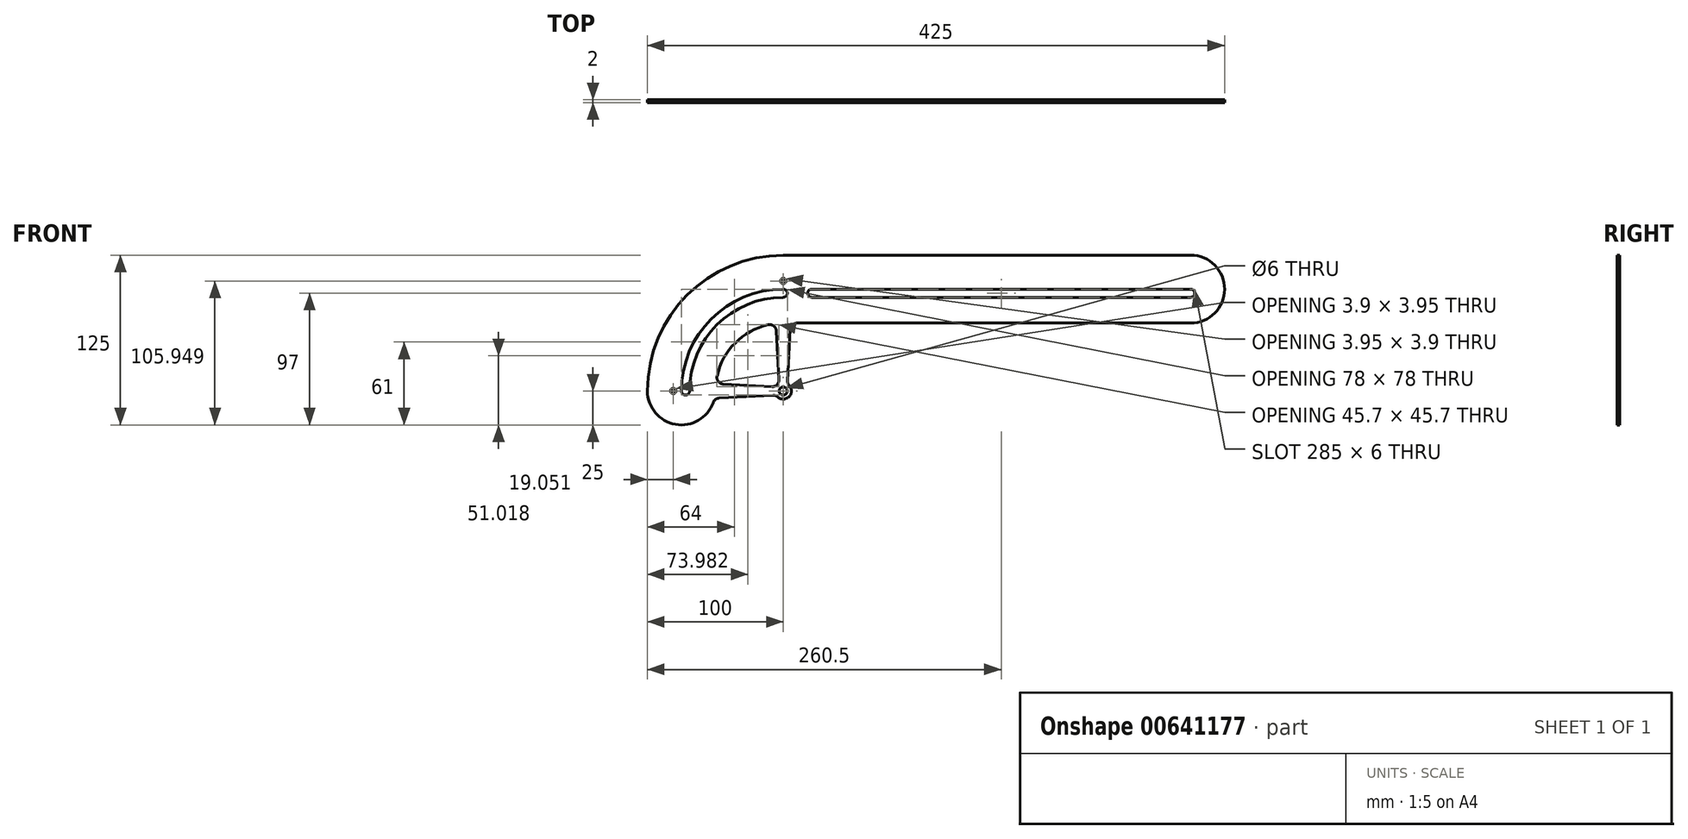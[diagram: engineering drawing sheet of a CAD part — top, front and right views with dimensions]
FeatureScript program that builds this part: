
annotation { "Feature Type Name" : "Feature", "Feature Type Description" : "" }
export const myFeature = defineFeature(function(context is Context, id is Id, definition is map)
    precondition{}
    {
        {
            var Q0;
            Q0=qCreatedBy(makeId("Front.planeOp"),FACE);
            var sketch = newSketch(context, id + "F0", { "sketchPlane" : qUnion([Q0])});
            skCircle(sketch, "E0", {"center": v(0, 0) * mm, "radius": 100 * mm, "construction": true});
            skCircle(sketch, "E1", {"center": v(0, 0) * mm, "radius": 75 * mm, "construction": true});
            skLineSegment(sketch, "E2", {"start": v(0, 0) * mm, "end": v(-100, 0) * mm, "construction": true});
            skLineSegment(sketch, "E3", {"start": v(0, 100) * mm, "end": v(300, 100) * mm});
            skArc(sketch, "E4", {"start": v(-50, 0) * mm, "mid": v(49.93, -2.67) * mm, "end": v(-49.71, 5.33) * mm, "construction": true});
            skLineSegment(sketch, "E5", {"start": v(0, 50) * mm, "end": v(300, 50) * mm});
            skCircle(sketch, "E6", {"center": v(-72, 0) * mm, "radius": 3 * mm});
            skCircle(sketch, "E7", {"center": v(0, 72) * mm, "radius": 3 * mm});
            skArc(sketch, "E8", {"start": v(-75, 0) * mm, "mid": v(-53.03, 53.03) * mm, "end": v(0, 75) * mm});
            skArc(sketch, "E9", {"start": v(-69, 0) * mm, "mid": v(-48.8, 48.8) * mm, "end": v(0, 69) * mm});
            skLineSegment(sketch, "E10", {"start": v(0, 75) * mm, "end": v(300, 75) * mm, "construction": true});
            skCircle(sketch, "E11", {"center": v(-75, 0) * mm, "radius": 25 * mm});
            skArc(sketch, "E12", {"start": v(-100, 0) * mm, "mid": v(-70.71, 70.71) * mm, "end": v(0, 100) * mm});
            skArc(sketch, "E13", {"start": v(-50, 0) * mm, "mid": v(-35.36, 35.36) * mm, "end": v(0, 50) * mm});
            skCircle(sketch, "E14", {"center": v(300, 72) * mm, "radius": 3 * mm});
            skCircle(sketch, "E15", {"center": v(21, 72) * mm, "radius": 3 * mm});
            skCircle(sketch, "E16", {"center": v(300, 75) * mm, "radius": 25 * mm});
            skCircle(sketch, "E17", {"center": v(0, 0) * mm, "radius": 6 * mm});
            skCircle(sketch, "E18", {"center": v(0, 0) * mm, "radius": 3 * mm});
            skLineSegment(sketch, "E19", {"start": v(-50.59, -5.38) * mm, "end": v(-5.2, -3) * mm});
            skLineSegment(sketch, "E20", {"start": v(-5.2, 3) * mm, "end": v(-49.71, 5.33) * mm});
            skLineSegment(sketch, "E21", {"start": v(-5.2, 3) * mm, "end": v(-5.2, -3) * mm, "construction": true});
            skLineSegment(sketch, "E22", {"start": v(0, 0) * mm, "end": v(0, 72) * mm, "construction": true});
            skLineSegment(sketch, "E23", {"start": v(-3, 5.2) * mm, "end": v(-5.33, 49.71) * mm});
            skLineSegment(sketch, "E24", {"start": v(3, 5.2) * mm, "end": v(5.35, 50) * mm});
            skLineSegment(sketch, "E25", {"start": v(-3, 5.2) * mm, "end": v(3, 5.2) * mm, "construction": true});
            skLineSegment(sketch, "E26", {"start": v(300, 75) * mm, "end": v(21, 75) * mm});
            skLineSegment(sketch, "E27", {"start": v(21, 69) * mm, "end": v(300, 69) * mm});
            skSolve(sketch);
        }
        {
            var Q0;
            {var subQ1=sQuery(id+"F0.wireOp",EDGE,"E6");var subQ6=sQuery(id+"F0.wireOp",EDGE,"E8");var subQ8=makeQuery(id+"F0.imprint","INTERSECT",VERTEX,{"derivedFrom":[subQ1,subQ6]});Q0=makeQuery(id+"F0.imprint","IMPRINT",FACE,{"disambiguationData":[TD([[makeQuery(id+"F0.imprint","IMPRINT",EDGE,{"disambiguationData":[TD([[subQ8,-1.0]])],"derivedFrom":subQ1}),-1.0]])]});}
            var Q1;
            {var subQ0=sQuery(id+"F0.wireOp",EDGE,"E19");Q1=makeQuery(id+"F0.imprint","IMPRINT",FACE,{"disambiguationData":[TD([[makeQuery(id+"F0.imprint","IMPRINT",EDGE,{"derivedFrom":subQ0}),1.0]])]});}
            var Q2;
            {var subQ11=sQuery(id+"F0.wireOp",EDGE,"E3");Q2=makeQuery(id+"F0.imprint","IMPRINT",FACE,{"disambiguationData":[TD([[makeQuery(id+"F0.imprint","IMPRINT",EDGE,{"derivedFrom":subQ11}),-1.0]])]});}
            var Q3;
            {var subQ0=sQuery(id+"F0.wireOp",EDGE,"E23");Q3=makeQuery(id+"F0.imprint","IMPRINT",FACE,{"disambiguationData":[TD([[makeQuery(id+"F0.imprint","IMPRINT",EDGE,{"derivedFrom":subQ0}),-1.0]])]});}
            var Q4;
            Q4=makeQuery(id+"F0.imprint","IMPRINT",FACE,{"disambiguationData":[TD([[makeQuery(id+"F0.imprint","IMPRINT",EDGE,{"derivedFrom":sQuery(id+"F0.wireOp",EDGE,"E18")}),-1.0]])]});
            var Q5;
            {var subQ0=sQuery(id+"F0.wireOp",EDGE,"E16");var subQ1=makeQuery(id+"F0.imprint","INTERSECT",VERTEX,{"derivedFrom":[sQuery(id+"F0.wireOp",EDGE,"E3"),subQ0]});Q5=makeQuery(id+"F0.imprint","IMPRINT",FACE,{"disambiguationData":[TD([[makeQuery(id+"F0.imprint","IMPRINT",EDGE,{"disambiguationData":[TD([[subQ1,-1.0]])],"derivedFrom":subQ0}),1.0]])]});}
            extrude(context, id + "F1", {"entities" : qUnion([Q0, Q1, Q2, Q3, Q4, Q5]), "depth" : 2 * mm, "offsetDistance" : 25 * mm, "symmetric" : true});
        }
        {
            var Q0;
            Q0=makeQuery(id+"F1.opExtrude","SWEPT_EDGE",EDGE,{"disambiguationData":[OSD([sQuery(id+"F0.wireOp",EDGE,"E13"),sQuery(id+"F0.wireOp",EDGE,"E20")])]});
            var Q1;
            Q1=makeQuery(id+"F1.opExtrude","SWEPT_EDGE",EDGE,{"disambiguationData":[OSD([sQuery(id+"F0.wireOp",EDGE,"E5"),sQuery(id+"F0.wireOp",EDGE,"E24")])]});
            var Q2;
            Q2=makeQuery(id+"F1.opExtrude","SWEPT_EDGE",EDGE,{"disambiguationData":[OSD([sQuery(id+"F0.wireOp",EDGE,"E13"),sQuery(id+"F0.wireOp",EDGE,"E23")])]});
            var Q3;
            Q3=makeQuery(id+"F1.opExtrude","SWEPT_EDGE",EDGE,{"disambiguationData":[OSD([sQuery(id+"F0.wireOp",EDGE,"E17"),sQuery(id+"F0.wireOp",EDGE,"E19")])]});
            var Q4;
            Q4=makeQuery(id+"F1.opExtrude","SWEPT_EDGE",EDGE,{"disambiguationData":[OSD([sQuery(id+"F0.wireOp",EDGE,"E11"),sQuery(id+"F0.wireOp",EDGE,"E19")])]});
            var Q5;
            Q5=makeQuery(id+"F1.opExtrude","SWEPT_EDGE",EDGE,{"disambiguationData":[OSD([sQuery(id+"F0.wireOp",EDGE,"E17"),sQuery(id+"F0.wireOp",EDGE,"E20")])]});
            var Q6;
            Q6=makeQuery(id+"F1.opExtrude","SWEPT_EDGE",EDGE,{"disambiguationData":[OSD([sQuery(id+"F0.wireOp",EDGE,"E17"),sQuery(id+"F0.wireOp",EDGE,"E23")])]});
            var Q7;
            Q7=makeQuery(id+"F1.opExtrude","SWEPT_EDGE",EDGE,{"disambiguationData":[OSD([sQuery(id+"F0.wireOp",EDGE,"E17"),sQuery(id+"F0.wireOp",EDGE,"E24")])]});
            fillet(context, id + "F2", {"entities" : qUnion([Q0, Q1, Q2, Q3, Q4, Q5, Q6, Q7]), "radius" : 5 * mm, "tangentPropagation" : true, "allowEdgeOverflow" : false});
        }
        {
            var Q0;
            {var subQ0=sQuery(id+"F0.wireOp",EDGE,"E17");Q0=makeQuery(id+"F2.opFillet","BLEND_EDGE",EDGE,{"blendedFrom":[makeQuery(id+"F1.opExtrude","SWEPT_EDGE",EDGE,{"disambiguationData":[OSD([subQ0,sQuery(id+"F0.wireOp",EDGE,"E20")])]}),makeQuery(id+"F1.opExtrude","SWEPT_EDGE",EDGE,{"disambiguationData":[OSD([subQ0,sQuery(id+"F0.wireOp",EDGE,"E23")])]})],"blendedInto":[]});}
            fillet(context, id + "F3", {"entities" : qUnion([Q0]), "radius" : 5 * mm, "tangentPropagation" : true, "allowEdgeOverflow" : false});
        }
        {
            var Q0;
            Q0=makeQuery(id+"F1.opExtrude","CAP_FACE",FACE,{"disambiguationData":[OSD([sQuery(id+"F0.wireOp",EDGE,"E3"),sQuery(id+"F0.wireOp",EDGE,"E5"),sQuery(id+"F0.wireOp",EDGE,"E6"),sQuery(id+"F0.wireOp",EDGE,"E7"),sQuery(id+"F0.wireOp",EDGE,"E8"),sQuery(id+"F0.wireOp",EDGE,"E9"),sQuery(id+"F0.wireOp",EDGE,"E11"),sQuery(id+"F0.wireOp",EDGE,"E12"),sQuery(id+"F0.wireOp",EDGE,"E13"),sQuery(id+"F0.wireOp",EDGE,"E14"),sQuery(id+"F0.wireOp",EDGE,"E15"),sQuery(id+"F0.wireOp",EDGE,"E16"),sQuery(id+"F0.wireOp",EDGE,"E17"),sQuery(id+"F0.wireOp",EDGE,"E18"),sQuery(id+"F0.wireOp",EDGE,"E19"),sQuery(id+"F0.wireOp",EDGE,"E20"),sQuery(id+"F0.wireOp",EDGE,"E23"),sQuery(id+"F0.wireOp",EDGE,"E24"),sQuery(id+"F0.wireOp",EDGE,"E26"),sQuery(id+"F0.wireOp",EDGE,"E27")])],"isStart":false});
            var sketch = newSketch(context, id + "F4", { "sketchPlane" : qUnion([Q0])});
            skLineSegment(sketch, "E28", {"start": v(0, 0) * mm, "end": v(-83, 0) * mm});
            skLineSegment(sketch, "E29.1.0", {"start": v(-77.17, 7.15) * mm, "end": v(-82.65, 7.66) * mm});
            skLineSegment(sketch, "E29.2.0", {"start": v(-76.18, 14.24) * mm, "end": v(-81.59, 15.25) * mm});
            skLineSegment(sketch, "E29.3.0", {"start": v(-74.54, 21.2) * mm, "end": v(-79.83, 22.71) * mm});
            skLineSegment(sketch, "E29.4.0", {"start": v(-72.27, 28) * mm, "end": v(-77.4, 29.98) * mm});
            skLineSegment(sketch, "E29.5.0", {"start": v(-69.38, 34.54) * mm, "end": v(-74.3, 37) * mm});
            skLineSegment(sketch, "E29.6.0", {"start": v(-65.9, 40.8) * mm, "end": v(-70.57, 43.7) * mm});
            skLineSegment(sketch, "E29.7.0", {"start": v(-61.85, 46.7) * mm, "end": v(-66.24, 50.02) * mm});
            skLineSegment(sketch, "E29.8.0", {"start": v(-57.27, 52.21) * mm, "end": v(-61.34, 55.92) * mm});
            skLineSegment(sketch, "E29.9.0", {"start": v(-52.21, 57.27) * mm, "end": v(-55.92, 61.34) * mm});
            skLineSegment(sketch, "E29.10.0", {"start": v(-46.7, 61.85) * mm, "end": v(-50.02, 66.24) * mm});
            skLineSegment(sketch, "E29.11.0", {"start": v(-40.8, 65.9) * mm, "end": v(-43.7, 70.57) * mm});
            skLineSegment(sketch, "E29.12.0", {"start": v(-34.54, 69.38) * mm, "end": v(-37, 74.3) * mm});
            skLineSegment(sketch, "E29.13.0", {"start": v(-28, 72.27) * mm, "end": v(-29.98, 77.4) * mm});
            skLineSegment(sketch, "E29.14.0", {"start": v(-21.2, 74.54) * mm, "end": v(-22.71, 79.83) * mm});
            skLineSegment(sketch, "E29.15.0", {"start": v(-14.24, 76.18) * mm, "end": v(-15.25, 81.59) * mm});
            skLineSegment(sketch, "E29.16.0", {"start": v(-7.15, 77.17) * mm, "end": v(-7.66, 82.65) * mm});
            skLineSegment(sketch, "E29.17.0", {"start": v(0, 0) * mm, "end": v(0, 83) * mm});
            skPoint(sketch, "E29.center", {"position": v(0, 0) * mm});
            skLineSegment(sketch, "E29.anchor1", {"start": v(0, 0) * mm, "end": v(-83, 0) * mm, "construction": true});
            skLineSegment(sketch, "E29.anchor2", {"start": v(0, 0) * mm, "end": v(0, 83) * mm, "construction": true});
            skCircle(sketch, "E30", {"center": v(0, 0) * mm, "radius": 77.5 * mm, "construction": true});
            skSolve(sketch);
        }
        {
            var Q0;
            {var subQ19=sQuery(id+"F0.wireOp",EDGE,"E3");Q0=makeQuery(id+"F4.imprint","IMPRINT",FACE,{"disambiguationData":[TD([[makeQuery(id+"F4.imprint","IMPRINT",EDGE,{"derivedFrom":makeQuery(id+"F1.opExtrude","CAP_EDGE",EDGE,{"disambiguationData":[OSD([subQ19])],"isStart":false})}),-1.0]])]});}
            var sketch = newSketch(context, id + "F5", { "sketchPlane" : qUnion([Q0])});
            skCircle(sketch, "E31", {"center": v(-81, 0) * mm, "radius": 2 * mm});
            skLineSegment(sketch, "E32", {"start": v(-82.9, 0.63) * mm, "end": v(-82, 0) * mm});
            skLineSegment(sketch, "E33", {"start": v(-82, 0) * mm, "end": v(-82.9, -0.63) * mm});
            skPoint(sketch, "E34.orphan", {"position": v(-83.85, 1.3) * mm});
            skPoint(sketch, "E35.orphan", {"position": v(-83.85, -1.3) * mm});
            skLineSegment(sketch, "E36", {"start": v(-82, 0) * mm, "end": v(-81, 0) * mm, "construction": true});
            skCircle(sketch, "E37.1.0", {"center": v(0, 81) * mm, "radius": 2 * mm});
            skLineSegment(sketch, "E37.1.1", {"start": v(0, 82) * mm, "end": v(-0.63, 82.9) * mm});
            skLineSegment(sketch, "E37.1.2", {"start": v(0.63, 82.9) * mm, "end": v(0, 82) * mm});
            skPoint(sketch, "E37.center", {"position": v(0, 0) * mm});
            skLineSegment(sketch, "E37.anchor1", {"start": v(0, 0) * mm, "end": v(-81, 0) * mm, "construction": true});
            skLineSegment(sketch, "E37.anchor2", {"start": v(0, 0) * mm, "end": v(0, 81) * mm, "construction": true});
            skSolve(sketch);
        }
        {
            var Q0;
            {var subQ0=sQuery(id+"F5.wireOp",EDGE,"E32");Q0=makeQuery(id+"F5.imprint","IMPRINT",FACE,{"disambiguationData":[TD([[makeQuery(id+"F5.imprint","IMPRINT",EDGE,{"derivedFrom":subQ0}),1.0]])]});}
            var Q1;
            {var subQ0=sQuery(id+"F5.wireOp",EDGE,"E37.1.1");Q1=makeQuery(id+"F5.imprint","IMPRINT",FACE,{"disambiguationData":[TD([[makeQuery(id+"F5.imprint","IMPRINT",EDGE,{"derivedFrom":subQ0}),1.0]])]});}
            extrude(context, id + "F6", {"entities" : qUnion([Q0, Q1]), "operationType" : NewBodyOperationType.REMOVE, "oppositeDirection" : true, "depth" : 25 * mm, "offsetDistance" : 25 * mm});
        }
    });
